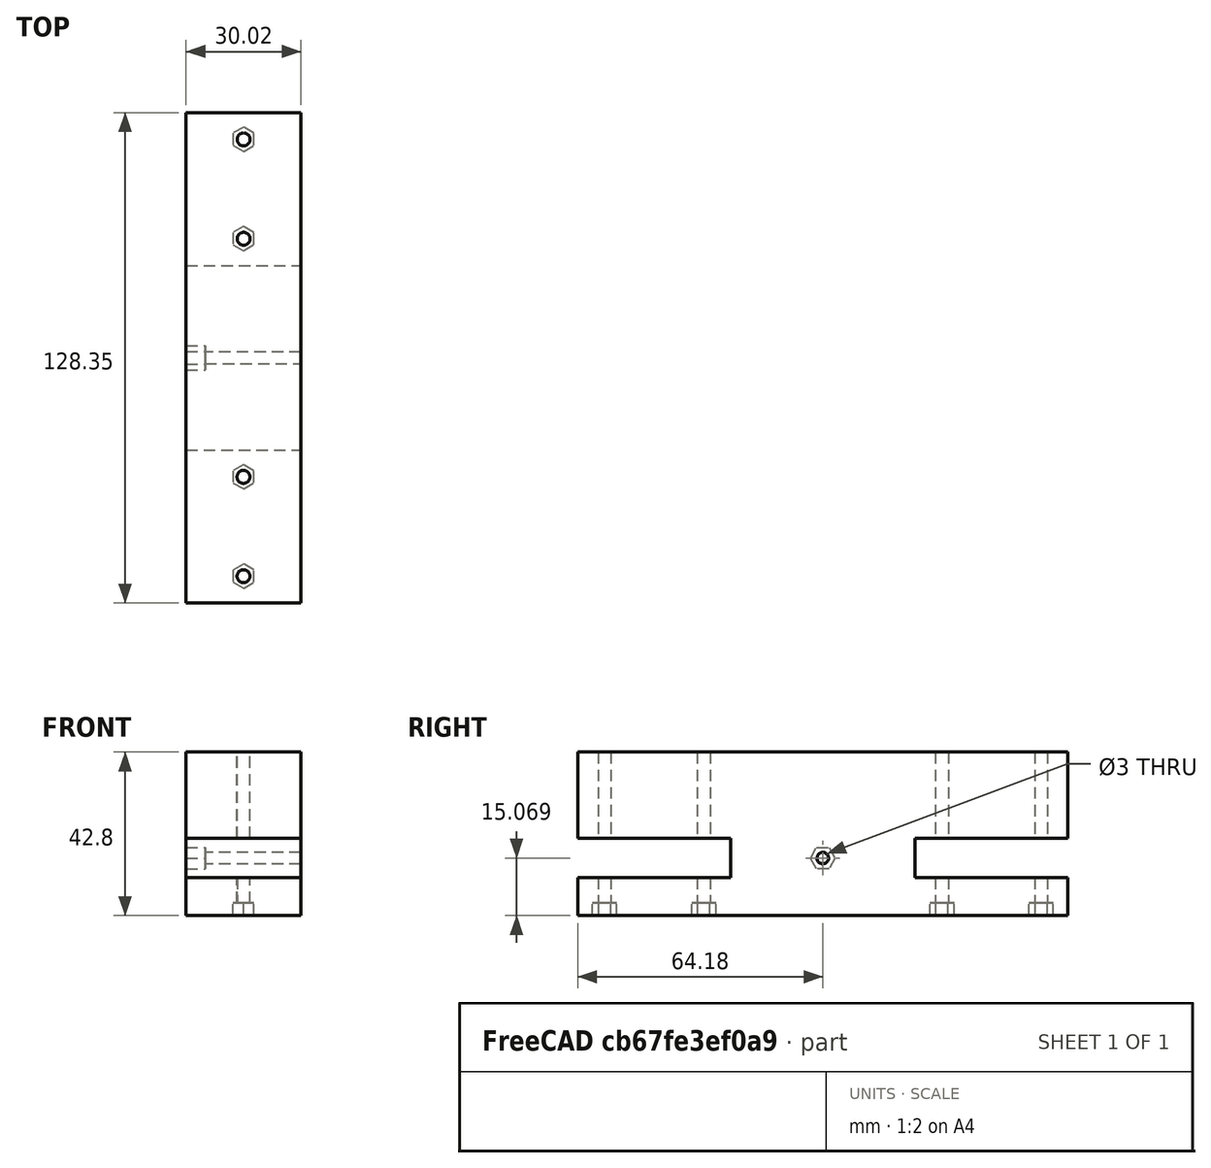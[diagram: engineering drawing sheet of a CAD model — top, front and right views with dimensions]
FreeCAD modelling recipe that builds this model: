
FCSTD DOCUMENT  (FreeCAD 2024.1R35694 (Git))
Label: frame_top_extender
License: All rights reserved
LicenseURL: http://en.wikipedia.org/wiki/All_rights_reserved
objects: Part::Feature×1, PartDesign::FeatureBase×1, Sketcher::SketchObject×1, PartDesign::Pocket×1, PartDesign::Body×1
note: 6 computed .brp shape members not serialized (recipe doc carries the construction recipe); baked Part::Feature solids carry a one-line shape summary decoded from their .brp

FEATURE [Part::Feature] Part__Feature  label="Pocket001"
  shape: bbox 30.03 x 128.4 x 42.8 mm, 65 faces (baked)
FEATURE [PartDesign::FeatureBase] BaseFeature
  BaseFeature = -> Part__Feature
FEATURE [Sketcher::SketchObject] Sketch
  FullyConstrained = false
  MapMode = 5
  Placement = pos=(-15.0149,0,0) rot=(0.57735,-0.57735,-0.57735;2.0944rad)
  Support = -> [BaseFeature]
  sketch-geometry (1):
    g0: Circle CenterX=0.000158 CenterY=0.018795 CenterZ=0 NormalX=0 NormalY=0 NormalZ=1 AngleXU=0 Radius=1.5
  constraints (1):
    c: Diameter(g0) = 3
FEATURE [PartDesign::Pocket] Pocket
  BaseFeature = -> BaseFeature
  Direction = (1,0,0)
  Length = 5
  Length2 = 5
  Profile = -> Sketch
  ReferenceAxis = -> Sketch [N_Axis]
  Refine = true
  Type = 1
FEATURE [PartDesign::Body] Body
  BaseFeature = -> Part__Feature
  Group = -> [BaseFeature,Sketch,Pocket]
  Origin = -> Origin
  Tip = -> Pocket
